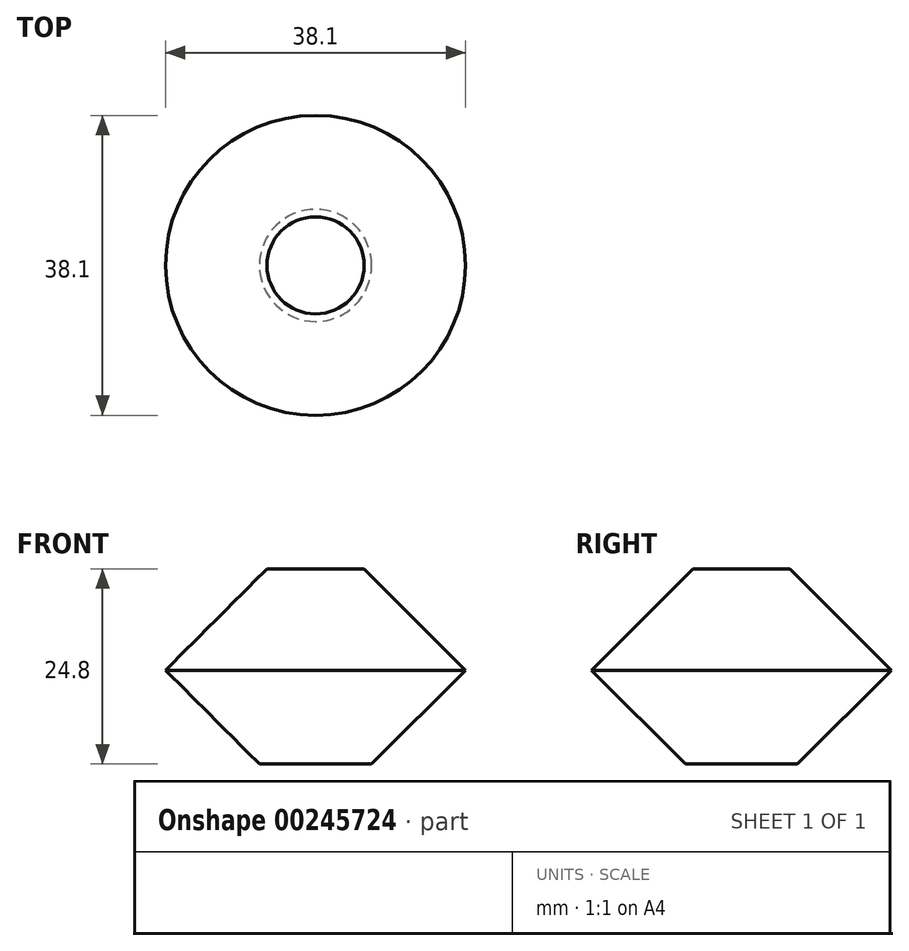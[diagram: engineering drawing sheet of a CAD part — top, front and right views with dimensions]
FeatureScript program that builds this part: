
annotation { "Feature Type Name" : "Feature", "Feature Type Description" : "" }
export const myFeature = defineFeature(function(context is Context, id is Id, definition is map)
    precondition{}
    {
        {
            var Q0;
            Q0=qCreatedBy(makeId("Front.planeOp"),FACE);
            var sketch = newSketch(context, id + "F0", { "sketchPlane" : qUnion([Q0])});
            skLineSegment(sketch, "E0", {"start": v(0, 11.92) * mm, "end": v(-19.05, 11.92) * mm, "construction": true});
            skLineSegment(sketch, "E1", {"start": v(-7.13, 0) * mm, "end": v(-19.05, 11.92) * mm});
            skLineSegment(sketch, "E2", {"start": v(-19.05, 11.92) * mm, "end": v(0, 30.97) * mm, "construction": true});
            skLineSegment(sketch, "E3", {"start": v(-19.05, 11.92) * mm, "end": v(-6.17, 24.8) * mm});
            skLineSegment(sketch, "E4", {"start": v(-6.17, 24.8) * mm, "end": v(0, 24.8) * mm});
            skLineSegment(sketch, "E5", {"start": v(0, 0) * mm, "end": v(0, 24.8) * mm});
            skLineSegment(sketch, "E6", {"start": v(-7.13, 0) * mm, "end": v(0, 0) * mm});
            skPoint(sketch, "E7.orphan", {"position": v(0, -7.13) * mm});
            skPoint(sketch, "E8", {"position": v(0, 30.97) * mm});
            skPoint(sketch, "E9", {"position": v(-5.98, 32.03) * mm});
            skLineSegment(sketch, "E10", {"start": v(0, 0) * mm, "end": v(-87, 0) * mm, "construction": true});
            skLineSegment(sketch, "E11", {"start": v(-19.05, 11.92) * mm, "end": v(-30.97, 0) * mm, "construction": true});
            skPoint(sketch, "E12", {"position": v(-30.97, 0) * mm});
            skSolve(sketch);
        }
        {
            var Q0;
            Q0=makeQuery(id+"F0.imprint","IMPRINT",FACE,{"disambiguationData":[TD([[makeQuery(id+"F0.imprint","IMPRINT",EDGE,{"derivedFrom":sQuery(id+"F0.wireOp",EDGE,"E1")}),-1.0]])]});
            var Q1;
            Q1=sQuery(id+"F0.wireOp",EDGE,"E5");
            revolve(context, id + "F1", {"entities" : qUnion([Q0]), "axis" : qUnion([Q1]), "revolveType" : RevolveType.FULL});
        }
    });
